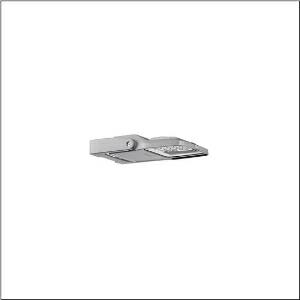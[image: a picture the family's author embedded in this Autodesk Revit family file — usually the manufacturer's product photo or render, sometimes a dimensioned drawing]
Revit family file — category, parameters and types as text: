
# Revit family: floodlight_fl_21_iq_micro___pl61_5xa7761a4c2a_08ca
name_source: partatom
category: Lighting Fixtures
units: mm (PartAtom-declared; Revit-internal decimal feet)

## family parameters
Cut with Voids When Loaded = No
Host = Face
Light Source = No
Part Type = Normal
Room Calculation Point = No
Round Connector Dimension = Use Diameter
Shared = No

## types (1)
- --- (1 x LED, 3030 lm, 23.1 W, 4000K)
    Apparent Load = 23 VA
    CIE Flux Codes = 33 65 98 100 100
    Color Rendering = 70
    Color Temperature = 4000K
    Default Elevation = 1800 mm
    Description = Floodlight FL 21 iQ micro, floodlight, primary light control with lens, of PMMA, primary optical cover: protective disc, of toughened safety glass, transparent, light distribution: PL61, light emission: direct distribution, installation type: surface-mounted, LED, High Power LED, rated luminous flux: 3.030lm, luminous efficacy: 131lm/W, light colour: 740, colour temperature: 4000K, control gear: iQ Comfort/DALI, control: optimised constant luminous flux control (CLO 2.0), Desk-Remote (wireless, voltage-free reading and setting of iQ features in the workshop via application-optimized NFC function/RFID function), Light-Fading, Smart-Wire, Night-Set, Lumen-Switch, Temp-Guard, Auto-Match, with terminal, 6-pole, mains connection: 220..240V, AC, 50/60Hz, start of lifetime: 23W, end of service life: 24W, reduction: 11W, luminaire housing, of diecast aluminium, powder-coated, Siteco® metallic grey (DB 702S), corrosivity category C5 mid according to DIN EN ISO 12944, suitable for swimming pools, chlorine-resistant, sealing non-destructively replaceable, design bracket, of diecast aluminium, powder-coated, Siteco® metallic grey (DB 702S), protection rating (complete): IP66, insulation class (complete): insulation class II (safety insulation), certification: CE, ENEC, VDE, protection symbol: D, impact resistance: IK07, permissible operating ambient temperature: -40..+40°C, permissible operating ambient temperature for outdoor applications: -40..+50°C, standard: DIN EN 12944, LABS conformity tested according to VDMA 24364:2018-05, packaging unit: 1 piece

Light Distribution: PL61
    Height = 65 mm
    Lamp = 1 x LED
    Lamp Light Flux = 3030 lm
    Lamp Power = 23.1 W
    Lamp count = 1
    Length = 312 mm
    Luminous efficacy = 131 lm/W
    Manufacturer = Siteco
    ModVariant = No
    Model = 5XA7761A4C2A
    Mounting Place = Wall
    Mounting Type = Surface mounted
    Number of Poles = 1
    OnlyDefault = Yes
    Power Factor = 1
    Product Name = Floodlight FL 21 iQ micro | PL61
    Product group = floodlight | wall mounted
    ProductGroupID = 2001
    Protection Class = Protection class II
    Protection Degree = IP 66
    RLX_Detail_Level = 1
    RLX_Emergency_Light_Flux = 0 lm
    RLX_Emergency_Type = 0
    RLX_Emergency_Type_DB = No
    RlxData = <blob elided: 97653 chars, md5=ce08240c>
    Socket = socket
    Standby Power = 0 W
    System Light Flux = 3030 lm
    System Power = 23 W
    Type Comments = factory setting: luminous flux: 100 % | dim-lin: 254 | 455 mA
    Type Image = l_1006878.jpg
    URL = http://relux.com
    VarID = @adj_194548
    Voltage = 0 V
    Weight = 0.00 kg
    Width = 230 mm

## geometry (parser evidence)
native form markers: Blend x4, Sweep x11
no freeform markers — native parametric forms only
